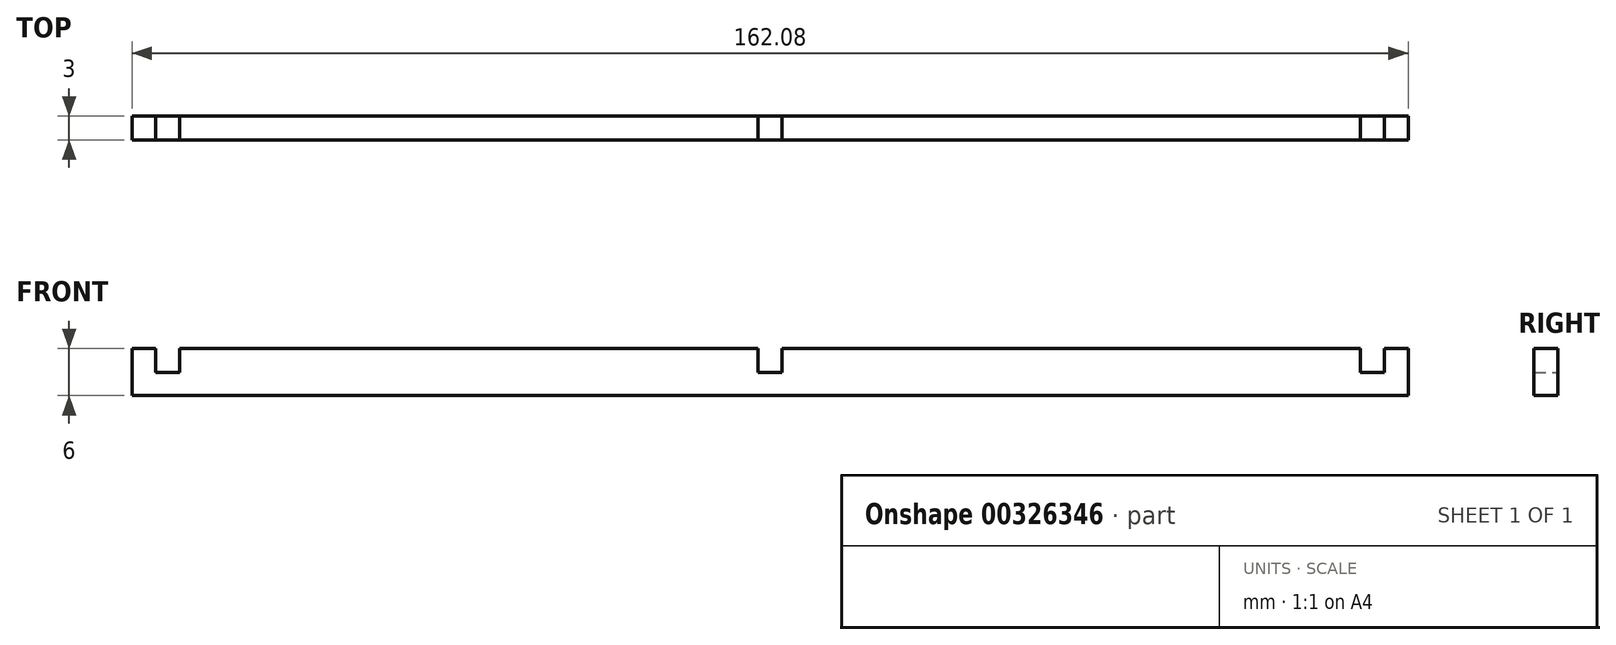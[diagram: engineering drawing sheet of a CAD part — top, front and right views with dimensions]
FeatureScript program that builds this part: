
annotation { "Feature Type Name" : "Feature", "Feature Type Description" : "" }
export const myFeature = defineFeature(function(context is Context, id is Id, definition is map)
    precondition{}
    {
        {
            var Q0;
            Q0=qCreatedBy(makeId("Front.planeOp"),FACE);
            var sketch = newSketch(context, id + "F0", { "sketchPlane" : qUnion([Q0])});
            skLineSegment(sketch, "E0", {"start": v(-81.04, 0) * mm, "end": v(-81.04, 6) * mm});
            skLineSegment(sketch, "E1", {"start": v(-81.04, 6) * mm, "end": v(-78.04, 6) * mm});
            skLineSegment(sketch, "E2", {"start": v(81.04, 6) * mm, "end": v(81.04, 0) * mm});
            skPoint(sketch, "E3", {"position": v(-78.04, 2.98) * mm});
            skPoint(sketch, "E4", {"position": v(-75, 2.98) * mm});
            skPoint(sketch, "E5", {"position": v(78.04, 2.98) * mm});
            skPoint(sketch, "E6", {"position": v(75, 2.98) * mm});
            skLineSegment(sketch, "E7", {"start": v(-75, 2.98) * mm, "end": v(-78.04, 2.98) * mm});
            skLineSegment(sketch, "E8", {"start": v(78.04, 2.98) * mm, "end": v(75, 2.98) * mm});
            skLineSegment(sketch, "E9", {"start": v(-81.04, 0) * mm, "end": v(81.04, 0) * mm});
            skLineSegment(sketch, "E10", {"start": v(78.04, 2.98) * mm, "end": v(78.04, 6) * mm});
            skLineSegment(sketch, "E11", {"start": v(75, 2.98) * mm, "end": v(75, 6) * mm});
            skLineSegment(sketch, "E12", {"start": v(-78.04, 2.98) * mm, "end": v(-78.04, 6) * mm});
            skLineSegment(sketch, "E13", {"start": v(-75, 2.98) * mm, "end": v(-75, 6) * mm});
            skLineSegment(sketch, "E14.trimOffspring", {"start": v(-75, 6) * mm, "end": v(-1.52, 6) * mm});
            skLineSegment(sketch, "E15.trimOffspring", {"start": v(78.04, 6) * mm, "end": v(81.04, 6) * mm});
            skLineSegment(sketch, "E16", {"start": v(-1.52, 6) * mm, "end": v(-1.52, 2.98) * mm});
            skLineSegment(sketch, "E17", {"start": v(-1.52, 2.98) * mm, "end": v(1.52, 2.98) * mm});
            skLineSegment(sketch, "E18", {"start": v(1.52, 2.98) * mm, "end": v(1.52, 6) * mm});
            skLineSegment(sketch, "E19.trimOffspring", {"start": v(1.52, 6) * mm, "end": v(75, 6) * mm});
            skSolve(sketch);
        }
        {
            var Q0;
            Q0=makeQuery(id+"F0.imprint","IMPRINT",FACE,{"disambiguationData":[TD([[makeQuery(id+"F0.imprint","IMPRINT",EDGE,{"derivedFrom":sQuery(id+"F0.wireOp",EDGE,"daeca98d-3240-409c-9885-89564d3c6af8")}),-1.0]])]});
            var Q1;
            Q1=makeQuery(id+"F0.imprint","IMPRINT",FACE,{"disambiguationData":[TD([[makeQuery(id+"F0.imprint","IMPRINT",EDGE,{"derivedFrom":sQuery(id+"F0.wireOp",EDGE,"E0")}),-1.0]])]});
            extrude(context, id + "F1", {"entities" : qUnion([Q0, Q1]), "depth" : 3 * mm});
        }
    });
